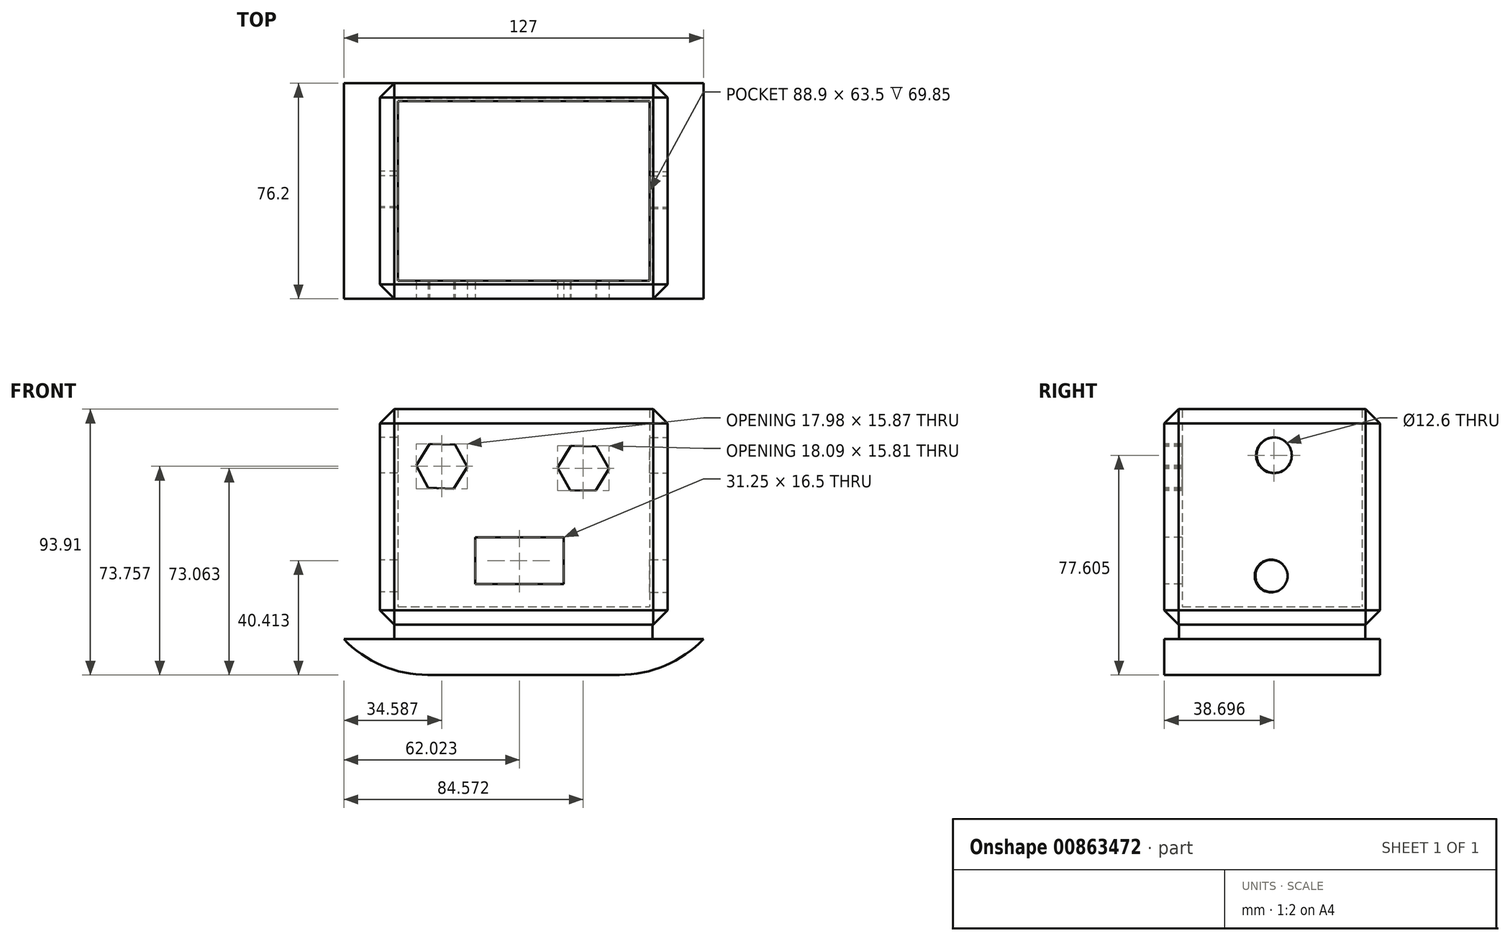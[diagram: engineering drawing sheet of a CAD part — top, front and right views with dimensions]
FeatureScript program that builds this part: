
annotation { "Feature Type Name" : "Feature", "Feature Type Description" : "" }
export const myFeature = defineFeature(function(context is Context, id is Id, definition is map)
    precondition{}
    {
        {
            var Q0;
            Q0=qCreatedBy(makeId("Front.planeOp"),FACE);
            var sketch = newSketch(context, id + "F0", { "sketchPlane" : qUnion([Q0])});
            skLineSegment(sketch, "E0.bottom", {"start": v(-46.03, 38.8) * mm, "end": v(55.57, 38.8) * mm});
            skLineSegment(sketch, "E0.top", {"start": v(-46.03, -37.4) * mm, "end": v(55.57, -37.4) * mm});
            skLineSegment(sketch, "E0.left", {"start": v(-46.03, 38.8) * mm, "end": v(-46.03, -37.4) * mm});
            skLineSegment(sketch, "E0.right", {"start": v(55.57, 38.8) * mm, "end": v(55.57, -37.4) * mm});
            skSolve(sketch);
        }
        {
            var Q0;
            Q0=makeQuery(id+"F0.imprint","IMPRINT",FACE,{"disambiguationData":[TD([[makeQuery(id+"F0.imprint","IMPRINT",EDGE,{"derivedFrom":sQuery(id+"F0.wireOp",EDGE,"E0.bottom")}),-1.0]])]});
            extrude(context, id + "F1", {"entities" : qUnion([Q0]), "depth" : 76.2 * mm, "offsetDistance" : 25.4 * mm});
        }
        {
            var Q0;
            Q0=makeQuery(id+"F1.opExtrude","SWEPT_FACE",FACE,{"disambiguationData":[OSD([sQuery(id+"F0.wireOp",EDGE,"E0.bottom")])]});
            shell(context, id + "F2", {"entities" : qUnion([Q0]), "thickness" : 6.35 * mm});
        }
        {
            var Q0;
            Q0=makeQuery(id+"F1.opExtrude","SWEPT_FACE",FACE,{"disambiguationData":[OSD([sQuery(id+"F0.wireOp",EDGE,"E0.right")])]});
            var sketch = newSketch(context, id + "F3", { "sketchPlane" : qUnion([Q0])});
            skCircle(sketch, "E1", {"center": v(-37.5, 22.5) * mm, "radius": 6.3 * mm});
            skLineSegment(sketch, "E2", {"start": v(-46.5, 9.98) * mm, "end": v(-28.1, 9.98) * mm, "construction": true});
            skSolve(sketch);
        }
        {
            var Q0;
            Q0=makeQuery(id+"F1.opExtrude","CAP_FACE",FACE,{"disambiguationData":[OSD([sQuery(id+"F0.wireOp",EDGE,"E0.bottom"),sQuery(id+"F0.wireOp",EDGE,"E0.top"),sQuery(id+"F0.wireOp",EDGE,"E0.left"),sQuery(id+"F0.wireOp",EDGE,"E0.right")])],"isStart":false});
            var sketch = newSketch(context, id + "F4", { "sketchPlane" : qUnion([Q0])});
            skCircle(sketch, "E3.cCircle", {"center": v(-24.23, 18.66) * mm, "radius": 7.79 * mm, "construction": true});
            skLineSegment(sketch, "E3.0", {"start": v(-15.25, 18.36) * mm, "end": v(-20, 10.72) * mm});
            skLineSegment(sketch, "E3.1", {"start": v(-20, 10.72) * mm, "end": v(-28.98, 11.02) * mm});
            skLineSegment(sketch, "E3.2", {"start": v(-28.98, 11.02) * mm, "end": v(-33.22, 18.96) * mm});
            skLineSegment(sketch, "E3.3", {"start": v(-33.22, 18.96) * mm, "end": v(-28.47, 26.6) * mm});
            skLineSegment(sketch, "E3.4", {"start": v(-28.47, 26.6) * mm, "end": v(-19.48, 26.3) * mm});
            skLineSegment(sketch, "E3.5", {"start": v(-19.48, 26.3) * mm, "end": v(-15.25, 18.36) * mm});
            skPoint(sketch, "E3.0.midPoint", {"position": v(-17.62, 14.54) * mm});
            skSolve(sketch);
        }
        {
            var Q0;
            Q0=makeQuery(id+"F4.imprint","IMPRINT",FACE,{"disambiguationData":[TD([[makeQuery(id+"F4.imprint","IMPRINT",EDGE,{"derivedFrom":sQuery(id+"F4.wireOp",EDGE,"E3.0")}),-1.0]])]});
            extrude(context, id + "F5", {"entities" : qUnion([Q0]), "operationType" : NewBodyOperationType.REMOVE, "oppositeDirection" : true, "depth" : 6.35 * mm, "offsetDistance" : 25.4 * mm});
        }
        {
            var Q0;
            Q0=makeQuery(id+"F1.opExtrude","CAP_FACE",FACE,{"disambiguationData":[OSD([sQuery(id+"F0.wireOp",EDGE,"E0.bottom"),sQuery(id+"F0.wireOp",EDGE,"E0.top"),sQuery(id+"F0.wireOp",EDGE,"E0.left"),sQuery(id+"F0.wireOp",EDGE,"E0.right")])],"isStart":false});
            var sketch = newSketch(context, id + "F6", { "sketchPlane" : qUnion([Q0])});
            skCircle(sketch, "E4.cCircle", {"center": v(25.75, 17.96) * mm, "radius": 7.83 * mm, "construction": true});
            skLineSegment(sketch, "E4.0", {"start": v(34.8, 17.81) * mm, "end": v(30.15, 10.06) * mm});
            skLineSegment(sketch, "E4.1", {"start": v(30.15, 10.06) * mm, "end": v(21.1, 10.2) * mm});
            skLineSegment(sketch, "E4.2", {"start": v(21.1, 10.2) * mm, "end": v(16.7, 18.11) * mm});
            skLineSegment(sketch, "E4.3", {"start": v(16.7, 18.11) * mm, "end": v(21.36, 25.87) * mm});
            skLineSegment(sketch, "E4.4", {"start": v(21.36, 25.87) * mm, "end": v(30.4, 25.72) * mm});
            skLineSegment(sketch, "E4.5", {"start": v(30.4, 25.72) * mm, "end": v(34.8, 17.81) * mm});
            skPoint(sketch, "E4.0.midPoint", {"position": v(32.47, 13.94) * mm});
            skSolve(sketch);
        }
        {
            var Q0;
            Q0=makeQuery(id+"F6.imprint","IMPRINT",FACE,{"disambiguationData":[TD([[makeQuery(id+"F6.imprint","IMPRINT",EDGE,{"derivedFrom":sQuery(id+"F6.wireOp",EDGE,"E4.0")}),-1.0]])]});
            extrude(context, id + "F7", {"entities" : qUnion([Q0]), "operationType" : NewBodyOperationType.REMOVE, "oppositeDirection" : true, "depth" : 6.35 * mm, "offsetDistance" : 25.4 * mm});
        }
        {
            var Q0;
            Q0=makeQuery(id+"F1.opExtrude","CAP_FACE",FACE,{"disambiguationData":[OSD([sQuery(id+"F0.wireOp",EDGE,"E0.bottom"),sQuery(id+"F0.wireOp",EDGE,"E0.top"),sQuery(id+"F0.wireOp",EDGE,"E0.left"),sQuery(id+"F0.wireOp",EDGE,"E0.right")])],"isStart":false});
            var sketch = newSketch(context, id + "F8", { "sketchPlane" : qUnion([Q0])});
            skLineSegment(sketch, "E5.bottom", {"start": v(-12.42, -6.44) * mm, "end": v(18.83, -6.44) * mm});
            skLineSegment(sketch, "E5.top", {"start": v(-12.42, -22.94) * mm, "end": v(18.83, -22.94) * mm});
            skLineSegment(sketch, "E5.left", {"start": v(-12.42, -6.44) * mm, "end": v(-12.42, -22.94) * mm});
            skLineSegment(sketch, "E5.right", {"start": v(18.83, -6.44) * mm, "end": v(18.83, -22.94) * mm});
            skSolve(sketch);
        }
        {
            var Q0;
            Q0=makeQuery(id+"F8.imprint","IMPRINT",FACE,{"disambiguationData":[TD([[makeQuery(id+"F8.imprint","IMPRINT",EDGE,{"derivedFrom":sQuery(id+"F8.wireOp",EDGE,"E5.bottom")}),-1.0]])]});
            extrude(context, id + "F9", {"entities" : qUnion([Q0]), "operationType" : NewBodyOperationType.REMOVE, "oppositeDirection" : true, "depth" : 6.35 * mm, "offsetDistance" : 25.4 * mm});
        }
        {
            var Q0;
            Q0=makeQuery(id+"F1.opExtrude","SWEPT_FACE",FACE,{"disambiguationData":[OSD([sQuery(id+"F0.wireOp",EDGE,"E0.top")])]});
            var sketch = newSketch(context, id + "F10", { "sketchPlane" : qUnion([Q0])});
            skLineSegment(sketch, "E6.bottom", {"start": v(-19.92, 56.32) * mm, "end": v(30.88, 56.32) * mm});
            skLineSegment(sketch, "E6.top", {"start": v(-19.92, 24.57) * mm, "end": v(30.88, 24.57) * mm});
            skLineSegment(sketch, "E6.left", {"start": v(-19.92, 56.32) * mm, "end": v(-19.92, 24.57) * mm});
            skLineSegment(sketch, "E6.right", {"start": v(30.88, 56.32) * mm, "end": v(30.88, 24.57) * mm});
            skSolve(sketch);
        }
        {
            var Q0;
            Q0 = qSketchRegion(id + "F10", true);
            extrude(context, id + "F11", {"entities" : qUnion([Q0]), "operationType" : NewBodyOperationType.ADD, "depth" : 5.08 * mm, "offsetDistance" : 25.4 * mm});
        }
        {
            var Q0;
            Q0=qCreatedBy(makeId("Front.planeOp"),FACE);
            var sketch = newSketch(context, id + "F12", { "sketchPlane" : qUnion([Q0])});
            skLineSegment(sketch, "E7.bottom", {"start": v(-58.82, -42.4) * mm, "end": v(68.18, -42.4) * mm});
            skLineSegment(sketch, "E7.top", {"start": v(-58.82, -55.1) * mm, "end": v(68.18, -55.1) * mm});
            skLineSegment(sketch, "E7.left", {"start": v(-58.82, -42.4) * mm, "end": v(-58.82, -55.1) * mm});
            skLineSegment(sketch, "E7.right", {"start": v(68.18, -42.4) * mm, "end": v(68.18, -55.1) * mm});
            skSolve(sketch);
        }
        {
            var Q0;
            Q0 = qSketchRegion(id + "F12", true);
            extrude(context, id + "F13", {"entities" : qUnion([Q0]), "operationType" : NewBodyOperationType.ADD, "depth" : 76.2 * mm, "offsetDistance" : 25.4 * mm});
        }
        {
            var Q0;
            Q0=makeQuery(id+"F13.opExtrude","SWEPT_EDGE",EDGE,{"disambiguationData":[OSD([sQuery(id+"F12.wireOp",EDGE,"E7.top"),sQuery(id+"F12.wireOp",EDGE,"E7.left")])]});
            fillet(context, id + "F14", {"entities" : qUnion([Q0]), "radius" : 41.1 * mm, "tangentPropagation" : true, "allowEdgeOverflow" : false});
        }
        {
            var Q0;
            Q0=makeQuery(id+"F13.opExtrude","SWEPT_EDGE",EDGE,{"disambiguationData":[OSD([sQuery(id+"F12.wireOp",EDGE,"E7.top"),sQuery(id+"F12.wireOp",EDGE,"E7.right")])]});
            fillet(context, id + "F15", {"entities" : qUnion([Q0]), "radius" : 41.1 * mm, "tangentPropagation" : true, "allowEdgeOverflow" : false});
        }
        {
            var Q0;
            Q0=qCreatedBy(makeId("Front.planeOp"),FACE);
            var sketch = newSketch(context, id + "F16", { "sketchPlane" : qUnion([Q0])});
            skLineSegment(sketch, "E8.bottom", {"start": v(-58.86, -55.36) * mm, "end": v(69.41, -55.36) * mm});
            skLineSegment(sketch, "E8.top", {"start": v(-58.86, -69.33) * mm, "end": v(69.41, -69.33) * mm});
            skLineSegment(sketch, "E8.left", {"start": v(-58.86, -55.36) * mm, "end": v(-58.86, -69.33) * mm});
            skLineSegment(sketch, "E8.right", {"start": v(69.41, -55.36) * mm, "end": v(69.41, -69.33) * mm});
            skSolve(sketch);
        }
        {
            var Q0;
            Q0 = qSketchRegion(id + "F16", true);
            extrude(context, id + "F17", {"entities" : qUnion([Q0]), "depth" : 76.2 * mm, "offsetDistance" : 25.4 * mm});
        }
        {
            var Q0;
            Q0=makeQuery(id+"F17.opExtrude","SWEPT_BODY",BODY,{"disambiguationData":[OSD([sQuery(id+"F16.wireOp",EDGE,"E8.bottom"),sQuery(id+"F16.wireOp",EDGE,"E8.top"),sQuery(id+"F16.wireOp",EDGE,"E8.left"),sQuery(id+"F16.wireOp",EDGE,"E8.right")])]});
            deleteBodies(context, id + "F18", {"entities" : qUnion([Q0])});
        }
        {
            var Q0;
            Q0=qCreatedBy(makeId("Right.planeOp"),FACE);
            var sketch = newSketch(context, id + "F19", { "sketchPlane" : qUnion([Q0])});
            skCircle(sketch, "E9", {"center": v(-37.33, 22.48) * mm, "radius": 6.5 * mm});
            skLineSegment(sketch, "E10", {"start": v(-28.48, 9.98) * mm, "end": v(-46.53, 9.98) * mm, "construction": true});
            skSolve(sketch);
        }
        {
            var Q0;
            Q0=makeQuery(id+"F3.imprint","IMPRINT",FACE,{"disambiguationData":[TD([[makeQuery(id+"F3.imprint","IMPRINT",EDGE,{"derivedFrom":sQuery(id+"F3.wireOp",EDGE,"E1")}),1.0]])]});
            var Q1;
            Q1=sQuery(id+"F19.wireOp",EDGE,"E9");
            extrude(context, id + "F20", {"entities" : qUnion([Q0]), "operationType" : NewBodyOperationType.REMOVE, "surfaceEntities" : qUnion([Q1]), "oppositeDirection" : true, "depth" : 6.35 * mm, "offsetDistance" : 25.4 * mm});
        }
        {
            var Q0;
            Q0=makeQuery(id+"F1.opExtrude","SWEPT_FACE",FACE,{"disambiguationData":[OSD([sQuery(id+"F0.wireOp",EDGE,"E0.left")])]});
            var sketch = newSketch(context, id + "F21", { "sketchPlane" : qUnion([Q0])});
            skCircle(sketch, "E11", {"center": v(37.33, 22.55) * mm, "radius": 6.27 * mm});
            skSolve(sketch);
        }
        {
            var Q0;
            Q0=makeQuery(id+"F21.imprint","IMPRINT",FACE,{"disambiguationData":[TD([[makeQuery(id+"F21.imprint","IMPRINT",EDGE,{"derivedFrom":sQuery(id+"F21.wireOp",EDGE,"E11")}),1.0]])]});
            extrude(context, id + "F22", {"entities" : qUnion([Q0]), "operationType" : NewBodyOperationType.REMOVE, "oppositeDirection" : true, "depth" : 6.35 * mm, "offsetDistance" : 25.4 * mm});
        }
        {
            var Q0;
            Q0=makeQuery(id+"F1.opExtrude","SWEPT_FACE",FACE,{"disambiguationData":[OSD([sQuery(id+"F0.wireOp",EDGE,"E0.left")])]});
            var sketch = newSketch(context, id + "F23", { "sketchPlane" : qUnion([Q0])});
            skCircle(sketch, "E12", {"center": v(38.36, -20.14) * mm, "radius": 5.7 * mm});
            skSolve(sketch);
        }
        {
            var Q0;
            Q0=makeQuery(id+"F23.imprint","IMPRINT",FACE,{"disambiguationData":[TD([[makeQuery(id+"F23.imprint","IMPRINT",EDGE,{"derivedFrom":sQuery(id+"F23.wireOp",EDGE,"E12")}),1.0]])]});
            extrude(context, id + "F24", {"entities" : qUnion([Q0]), "operationType" : NewBodyOperationType.REMOVE, "oppositeDirection" : true, "depth" : 6.35 * mm, "offsetDistance" : 25.4 * mm});
        }
        {
            var Q0;
            Q0=makeQuery(id+"F3.imprint","IMPRINT",FACE,{"disambiguationData":[TD([[makeQuery(id+"F3.imprint","IMPRINT",EDGE,{"derivedFrom":sQuery(id+"F3.wireOp",EDGE,"E1")}),-1.0]])]});
            var sketch = newSketch(context, id + "F25", { "sketchPlane" : qUnion([Q0])});
            skCircle(sketch, "E13", {"center": v(-38.51, -20.14) * mm, "radius": 5.8 * mm});
            skSolve(sketch);
        }
        {
            var Q0;
            Q0 = qSketchRegion(id + "F25", true);
            extrude(context, id + "F26", {"entities" : qUnion([Q0]), "operationType" : NewBodyOperationType.REMOVE, "oppositeDirection" : true, "depth" : 6.35 * mm, "offsetDistance" : 25.4 * mm});
        }
        {
            var Q0;
            Q0=makeQuery(id+"F2.opShell","OFFSET_FACE",FACE,{"disambiguationData":[OSD([sQuery(id+"F0.wireOp",EDGE,"E0.top")])]});
            var sketch = newSketch(context, id + "F27", { "sketchPlane" : qUnion([Q0])});
            skCircle(sketch, "E14.cCircle", {"center": v(0, -40.8) * mm, "radius": 11.15 * mm, "construction": true});
            skLineSegment(sketch, "E14.0", {"start": v(12.87, -41) * mm, "end": v(6.26, -52.04) * mm});
            skLineSegment(sketch, "E14.1", {"start": v(6.26, -52.04) * mm, "end": v(-6.61, -51.84) * mm});
            skLineSegment(sketch, "E14.2", {"start": v(-6.61, -51.84) * mm, "end": v(-12.87, -40.59) * mm});
            skLineSegment(sketch, "E14.3", {"start": v(-12.87, -40.59) * mm, "end": v(-6.26, -29.55) * mm});
            skLineSegment(sketch, "E14.4", {"start": v(-6.26, -29.55) * mm, "end": v(6.61, -29.75) * mm});
            skLineSegment(sketch, "E14.5", {"start": v(6.61, -29.75) * mm, "end": v(12.87, -41) * mm});
            skPoint(sketch, "E14.0.midPoint", {"position": v(9.56, -46.52) * mm});
            skSolve(sketch);
        }
        {
            var Q0;
            Q0=makeQuery(id+"F27.imprint","IMPRINT",FACE,{"disambiguationData":[TD([[makeQuery(id+"F27.imprint","IMPRINT",EDGE,{"derivedFrom":sQuery(id+"F27.wireOp",EDGE,"E14.0")}),-1.0]])]});
            extrude(context, id + "F28", {"entities" : qUnion([Q0]), "depth" : 104.14 * mm, "offsetDistance" : 25.4 * mm});
        }
        {
            var Q0;
            Q0=makeQuery(id+"F28.opExtrude","SWEPT_BODY",BODY,{"disambiguationData":[OSD([sQuery(id+"F27.wireOp",EDGE,"E14.0"),sQuery(id+"F27.wireOp",EDGE,"E14.1"),sQuery(id+"F27.wireOp",EDGE,"E14.2"),sQuery(id+"F27.wireOp",EDGE,"E14.3"),sQuery(id+"F27.wireOp",EDGE,"E14.4"),sQuery(id+"F27.wireOp",EDGE,"E14.5")])]});
            deleteBodies(context, id + "F29", {"entities" : qUnion([Q0])});
        }
        {
            var Q0;
            Q0=makeQuery(id+"F11.opExtrude","SWEPT_FACE",FACE,{"disambiguationData":[OSD([sQuery(id+"F10.wireOp",EDGE,"E6.bottom")])]});
            extrude(context, id + "F30", {"entities" : qUnion([Q0]), "operationType" : NewBodyOperationType.ADD, "depth" : 10.92 * mm, "offsetDistance" : 25.4 * mm});
        }
        {
            var Q0;
            {var subQ0=sQuery(id+"F10.wireOp",EDGE,"E6.right");Q0=makeQuery(id+"F30.boolean.opBoolean","MERGE",FACE,{"derivedFrom":[makeQuery(id+"F11.opExtrude","SWEPT_FACE",FACE,{"disambiguationData":[OSD([subQ0])]}),makeQuery(id+"F30.opExtrude","SWEPT_FACE",FACE,{"disambiguationData":[OSD([sQuery(id+"F10.wireOp",EDGE,"E6.bottom"),subQ0])]})]});}
            extrude(context, id + "F31", {"entities" : qUnion([Q0]), "operationType" : NewBodyOperationType.ADD, "depth" : 19.3 * mm, "offsetDistance" : 25.4 * mm});
        }
        {
            var Q0;
            {var subQ0=sQuery(id+"F10.wireOp",EDGE,"E6.right");var subQ1=sQuery(id+"F10.wireOp",EDGE,"E6.bottom");Q0=makeQuery(id+"F31.boolean.opBoolean","MERGE",FACE,{"derivedFrom":[makeQuery(id+"F30.opExtrude","CAP_FACE",FACE,{"disambiguationData":[OSD([subQ1])],"isStart":false}),makeQuery(id+"F31.opExtrude","SWEPT_FACE",FACE,{"disambiguationData":[OSD([subQ1,subQ0]),TDD([makeQuery(id+"F30.opExtrude","CAP_EDGE",EDGE,{"disambiguationData":[OSD([subQ1,subQ0])],"isStart":false})])]})]});}
            extrude(context, id + "F32", {"entities" : qUnion([Q0]), "operationType" : NewBodyOperationType.ADD, "depth" : 3.8 * mm, "offsetDistance" : 25.4 * mm});
        }
        {
            var Q0;
            {var subQ0=sQuery(id+"F10.wireOp",EDGE,"E6.left");var subQ1=sQuery(id+"F10.wireOp",EDGE,"E6.bottom");Q0=makeQuery(id+"F32.boolean.opBoolean","MERGE",FACE,{"derivedFrom":[makeQuery(id+"F30.boolean.opBoolean","MERGE",FACE,{"derivedFrom":[makeQuery(id+"F11.opExtrude","SWEPT_FACE",FACE,{"disambiguationData":[OSD([subQ0])]}),makeQuery(id+"F30.opExtrude","SWEPT_FACE",FACE,{"disambiguationData":[OSD([subQ1,subQ0])]})]}),makeQuery(id+"F32.opExtrude","SWEPT_FACE",FACE,{"disambiguationData":[OSD([subQ1,subQ0])]})]});}
            extrude(context, id + "F33", {"entities" : qUnion([Q0]), "operationType" : NewBodyOperationType.ADD, "depth" : 21.08 * mm, "offsetDistance" : 25.4 * mm});
        }
        {
            var Q0;
            {var subQ0=sQuery(id+"F10.wireOp",EDGE,"E6.top");Q0=makeQuery(id+"F33.boolean.opBoolean","MERGE",FACE,{"derivedFrom":[makeQuery(id+"F31.boolean.opBoolean","MERGE",FACE,{"derivedFrom":[makeQuery(id+"F11.opExtrude","SWEPT_FACE",FACE,{"disambiguationData":[OSD([subQ0])]}),makeQuery(id+"F31.opExtrude","SWEPT_FACE",FACE,{"disambiguationData":[OSD([subQ0,sQuery(id+"F10.wireOp",EDGE,"E6.right")])]})]}),makeQuery(id+"F33.opExtrude","SWEPT_FACE",FACE,{"disambiguationData":[OSD([subQ0,sQuery(id+"F10.wireOp",EDGE,"E6.left")])]})]});}
            extrude(context, id + "F34", {"entities" : qUnion([Q0]), "operationType" : NewBodyOperationType.ADD, "depth" : 19.3 * mm, "offsetDistance" : 25.4 * mm});
        }
        {
            var Q0;
            Q0=makeQuery(id+"F1.opExtrude","CAP_EDGE",EDGE,{"disambiguationData":[OSD([sQuery(id+"F0.wireOp",EDGE,"E0.bottom")])],"isStart":false});
            var Q1;
            Q1=makeQuery(id+"F1.opExtrude","CAP_EDGE",EDGE,{"disambiguationData":[OSD([sQuery(id+"F0.wireOp",EDGE,"E0.left")])],"isStart":false});
            var Q2;
            Q2=makeQuery(id+"F1.opExtrude","CAP_EDGE",EDGE,{"disambiguationData":[OSD([sQuery(id+"F0.wireOp",EDGE,"E0.top")])],"isStart":false});
            var Q3;
            Q3=makeQuery(id+"F1.opExtrude","CAP_EDGE",EDGE,{"disambiguationData":[OSD([sQuery(id+"F0.wireOp",EDGE,"E0.right")])],"isStart":false});
            var Q4;
            Q4=makeQuery(id+"F1.opExtrude","SWEPT_EDGE",EDGE,{"disambiguationData":[OSD([sQuery(id+"F0.wireOp",EDGE,"E0.bottom"),sQuery(id+"F0.wireOp",EDGE,"E0.right")])]});
            var Q5;
            Q5=makeQuery(id+"F1.opExtrude","SWEPT_EDGE",EDGE,{"disambiguationData":[OSD([sQuery(id+"F0.wireOp",EDGE,"E0.top"),sQuery(id+"F0.wireOp",EDGE,"E0.right")])]});
            var Q6;
            Q6=makeQuery(id+"F1.opExtrude","CAP_EDGE",EDGE,{"disambiguationData":[OSD([sQuery(id+"F0.wireOp",EDGE,"E0.right")])],"isStart":true});
            var Q7;
            Q7=makeQuery(id+"F1.opExtrude","CAP_EDGE",EDGE,{"disambiguationData":[OSD([sQuery(id+"F0.wireOp",EDGE,"E0.bottom")])],"isStart":true});
            var Q8;
            Q8=makeQuery(id+"F1.opExtrude","CAP_EDGE",EDGE,{"disambiguationData":[OSD([sQuery(id+"F0.wireOp",EDGE,"E0.top")])],"isStart":true});
            var Q9;
            Q9=makeQuery(id+"F1.opExtrude","CAP_EDGE",EDGE,{"disambiguationData":[OSD([sQuery(id+"F0.wireOp",EDGE,"E0.left")])],"isStart":true});
            var Q10;
            Q10=makeQuery(id+"F1.opExtrude","SWEPT_EDGE",EDGE,{"disambiguationData":[OSD([sQuery(id+"F0.wireOp",EDGE,"E0.bottom"),sQuery(id+"F0.wireOp",EDGE,"E0.left")])]});
            var Q11;
            Q11=makeQuery(id+"F1.opExtrude","SWEPT_EDGE",EDGE,{"disambiguationData":[OSD([sQuery(id+"F0.wireOp",EDGE,"E0.top"),sQuery(id+"F0.wireOp",EDGE,"E0.left")])]});
            chamfer(context, id + "F35", {"entities" : qUnion([Q0, Q1, Q2, Q3, Q4, Q5, Q6, Q7, Q8, Q9, Q10, Q11]), "width" : 5.08 * mm, "tangentPropagation" : true});
        }
    });
